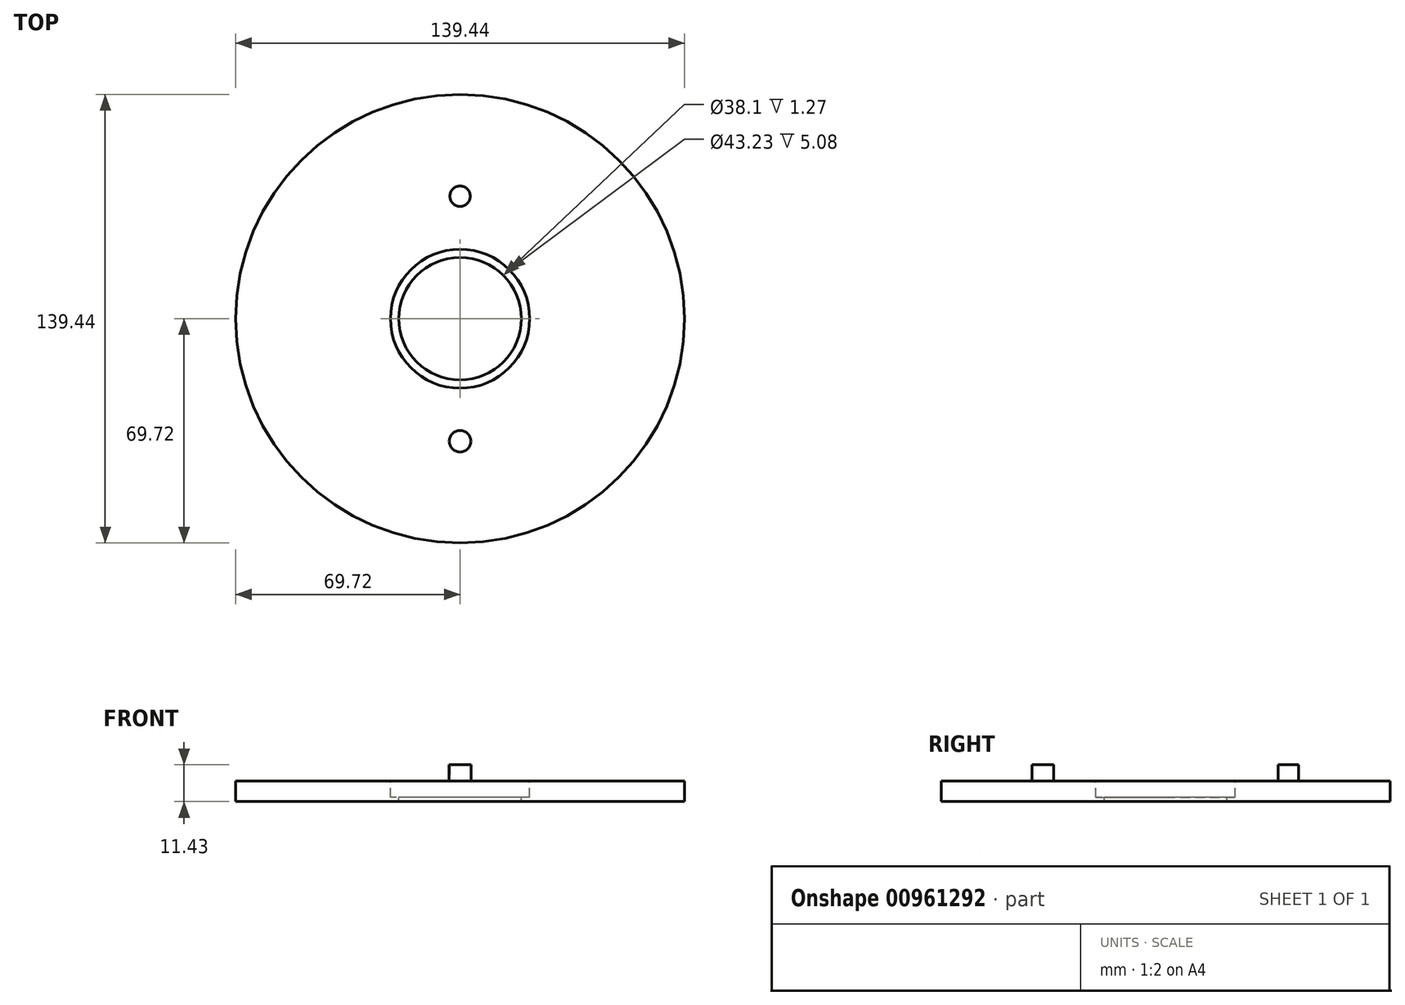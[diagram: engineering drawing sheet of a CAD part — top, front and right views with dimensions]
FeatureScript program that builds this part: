
annotation { "Feature Type Name" : "Feature", "Feature Type Description" : "" }
export const myFeature = defineFeature(function(context is Context, id is Id, definition is map)
    precondition{}
    {
        {
            var Q0;
            Q0=qCreatedBy(makeId("Top.planeOp"),FACE);
            var sketch = newSketch(context, id + "F0", { "sketchPlane" : qUnion([Q0])});
            skCircle(sketch, "E0", {"center": v(0, 0) * mm, "radius": 69.72 * mm});
            skSolve(sketch);
        }
        {
            var Q0;
            Q0 = qSketchRegion(id + "F0", true);
            extrude(context, id + "F1", {"entities" : qUnion([Q0]), "depth" : 6.35 * mm, "offsetDistance" : 25.4 * mm});
        }
        {
            var Q0;
            Q0=makeQuery(id+"F1.opExtrude","CAP_FACE",FACE,{"disambiguationData":[OSD([sQuery(id+"F0.wireOp",EDGE,"E0")])],"isStart":false});
            var sketch = newSketch(context, id + "F2", { "sketchPlane" : qUnion([Q0])});
            skCircle(sketch, "E1", {"center": v(0, 0) * mm, "radius": 19.05 * mm});
            skSolve(sketch);
        }
        {
            var Q0;
            Q0 = qSketchRegion(id + "F2", true);
            extrude(context, id + "F3", {"entities" : qUnion([Q0]), "operationType" : NewBodyOperationType.REMOVE, "oppositeDirection" : true, "depth" : 25.4 * mm, "offsetDistance" : 25.4 * mm});
        }
        {
            var Q0;
            Q0=makeQuery(id+"F1.opExtrude","CAP_FACE",FACE,{"disambiguationData":[OSD([sQuery(id+"F0.wireOp",EDGE,"E0")])],"isStart":false});
            var sketch = newSketch(context, id + "F4", { "sketchPlane" : qUnion([Q0])});
            skCircle(sketch, "E2", {"center": v(0, 0) * mm, "radius": 21.61 * mm});
            skSolve(sketch);
        }
        {
            var Q0;
            Q0 = qSketchRegion(id + "F4", true);
            extrude(context, id + "F5", {"entities" : qUnion([Q0]), "operationType" : NewBodyOperationType.REMOVE, "oppositeDirection" : true, "depth" : 3.3 * mm, "offsetDistance" : 25.4 * mm});
        }
        {
            var Q0;
            Q0=makeQuery(id+"F5.boolean.opBoolean","COPY",FACE,{"derivedFrom":makeQuery(id+"F5.opExtrude","CAP_FACE",FACE,{"disambiguationData":[OSD([sQuery(id+"F4.wireOp",EDGE,"E2")])],"isStart":false})});
            extrude(context, id + "F6", {"entities" : qUnion([Q0]), "operationType" : NewBodyOperationType.REMOVE, "oppositeDirection" : true, "depth" : 1.78 * mm, "offsetDistance" : 25.4 * mm});
        }
        {
            var Q0;
            Q0=makeQuery(id+"F1.opExtrude","CAP_FACE",FACE,{"disambiguationData":[OSD([sQuery(id+"F0.wireOp",EDGE,"E0")])],"isStart":false});
            var sketch = newSketch(context, id + "F7", { "sketchPlane" : qUnion([Q0])});
            skCircle(sketch, "E3", {"center": v(0, 38.1) * mm, "radius": 3.17 * mm});
            skCircle(sketch, "E4", {"center": v(0, -38.1) * mm, "radius": 3.36 * mm});
            skSolve(sketch);
        }
        {
            var Q0;
            Q0=makeQuery(id+"F7.imprint","IMPRINT",FACE,{"disambiguationData":[TD([[makeQuery(id+"F7.imprint","IMPRINT",EDGE,{"derivedFrom":sQuery(id+"F7.wireOp",EDGE,"E3")}),1.0]])]});
            var Q1;
            Q1=makeQuery(id+"F7.imprint","IMPRINT",FACE,{"disambiguationData":[TD([[makeQuery(id+"F7.imprint","IMPRINT",EDGE,{"derivedFrom":sQuery(id+"F7.wireOp",EDGE,"E4")}),1.0]])]});
            extrude(context, id + "F8", {"entities" : qUnion([Q0, Q1]), "operationType" : NewBodyOperationType.ADD, "depth" : 5.08 * mm, "offsetDistance" : 25.4 * mm});
        }
    });
